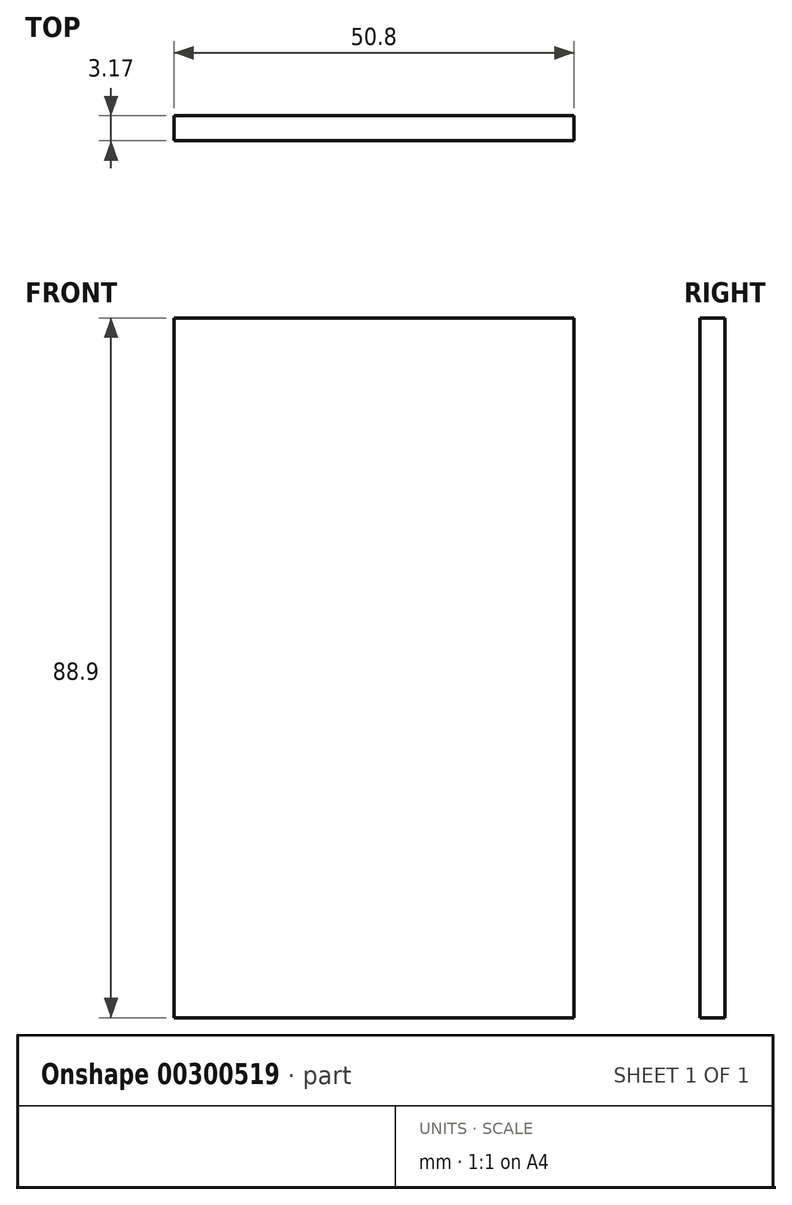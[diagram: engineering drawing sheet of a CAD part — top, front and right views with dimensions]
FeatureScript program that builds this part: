
annotation { "Feature Type Name" : "Feature", "Feature Type Description" : "" }
export const myFeature = defineFeature(function(context is Context, id is Id, definition is map)
    precondition{}
    {
        {
            var Q0;
            Q0=qCreatedBy(makeId("Front.planeOp"),FACE);
            var sketch = newSketch(context, id + "F0", { "sketchPlane" : qUnion([Q0])});
            skLineSegment(sketch, "E0.bottom", {"start": v(-25.4, -44.45) * mm, "end": v(25.4, -44.45) * mm});
            skLineSegment(sketch, "E0.top", {"start": v(-25.4, 44.45) * mm, "end": v(25.4, 44.45) * mm});
            skLineSegment(sketch, "E0.left", {"start": v(-25.4, -44.45) * mm, "end": v(-25.4, 44.45) * mm});
            skLineSegment(sketch, "E0.right", {"start": v(25.4, -44.45) * mm, "end": v(25.4, 44.45) * mm});
            skPoint(sketch, "E0.middle", {"position": v(0, 0) * mm});
            skSolve(sketch);
        }
        {
            var Q0;
            Q0 = qSketchRegion(id + "F0", true);
            extrude(context, id + "F1", {"entities" : qUnion([Q0]), "depth" : 3.17 * mm});
        }
    });
